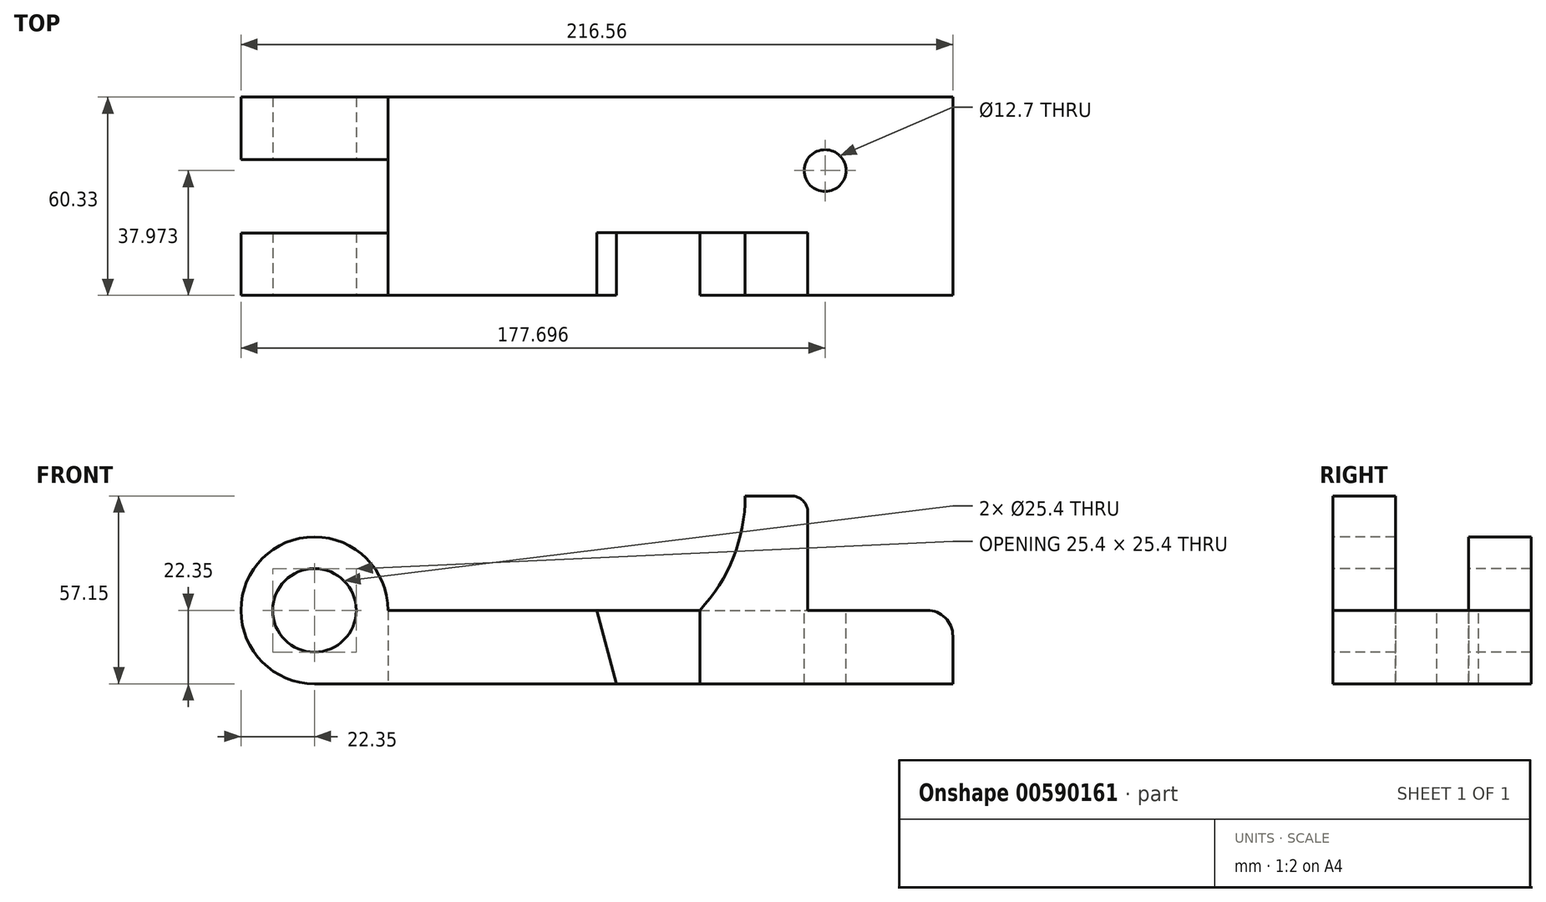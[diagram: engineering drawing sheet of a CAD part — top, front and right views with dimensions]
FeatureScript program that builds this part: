
annotation { "Feature Type Name" : "Feature", "Feature Type Description" : "" }
export const myFeature = defineFeature(function(context is Context, id is Id, definition is map)
    precondition{}
    {
        {
            var Q0;
            Q0=qCreatedBy(makeId("Front.planeOp"),FACE);
            var sketch = newSketch(context, id + "F0", { "sketchPlane" : qUnion([Q0])});
            skCircle(sketch, "E0", {"center": v(0, 0) * mm, "radius": 22.35 * mm});
            skCircle(sketch, "E1", {"center": v(0, 0) * mm, "radius": 12.7 * mm});
            skLineSegment(sketch, "E2", {"start": v(0, -22.35) * mm, "end": v(91.85, -22.35) * mm});
            skLineSegment(sketch, "E3", {"start": v(91.85, -22.35) * mm, "end": v(117.25, -22.35) * mm});
            skLineSegment(sketch, "E4", {"start": v(117.25, -22.35) * mm, "end": v(194.2, -22.35) * mm});
            skLineSegment(sketch, "E5", {"start": v(0, 62.8) * mm, "end": v(0, -59.04) * mm, "construction": true});
            skLineSegment(sketch, "E6", {"start": v(22.35, 0) * mm, "end": v(85.85, 0) * mm});
            skLineSegment(sketch, "E7", {"start": v(85.85, 0) * mm, "end": v(91.85, -22.35) * mm});
            skLineSegment(sketch, "E8", {"start": v(117.25, 0) * mm, "end": v(117.25, -22.35) * mm});
            skLineSegment(sketch, "E9", {"start": v(85.85, 0) * mm, "end": v(117.25, 0) * mm});
            skPoint(sketch, "E10", {"position": v(-22.35, 0) * mm});
            skLineSegment(sketch, "E11", {"start": v(194.2, -22.35) * mm, "end": v(194.2, -7.87) * mm});
            skPoint(sketch, "E11.endSnap0", {"position": v(54.1, 0) * mm});
            skLineSegment(sketch, "E12", {"start": v(186.33, 0) * mm, "end": v(150.09, 0) * mm});
            skLineSegment(sketch, "E13", {"start": v(150.09, 0) * mm, "end": v(150.09, 29.72) * mm});
            skLineSegment(sketch, "E14", {"start": v(145, 34.8) * mm, "end": v(131.04, 34.8) * mm});
            skArc(sketch, "E15", {"start": v(117.25, 0) * mm, "mid": v(127.46, 16.08) * mm, "end": v(131.04, 34.8) * mm});
            skPoint(sketch, "E16.visualSharp", {"position": v(150.09, 34.8) * mm});
            skArc(sketch, "E16.filletArc", {"start": v(150.09, 29.72) * mm, "mid": v(148.6, 33.31) * mm, "end": v(145, 34.8) * mm});
            skPoint(sketch, "E17.visualSharp", {"position": v(194.2, 0) * mm});
            skArc(sketch, "E17.filletArc", {"start": v(194.2, -7.87) * mm, "mid": v(191.9, -2.3) * mm, "end": v(186.33, 0) * mm});
            skLineSegment(sketch, "E18", {"start": v(117.25, 0) * mm, "end": v(150.09, 0) * mm});
            skSolve(sketch);
        }
        {
            var Q0;
            Q0=makeQuery(id+"F0.imprint","IMPRINT",FACE,{"disambiguationData":[TD([[makeQuery(id+"F0.imprint","IMPRINT",EDGE,{"derivedFrom":sQuery(id+"F0.wireOp",EDGE,"E1")}),-1.0]])]});
            extrude(context, id + "F1", {"entities" : qUnion([Q0]), "oppositeDirection" : true, "depth" : 60.32 * mm, "offsetDistance" : 25.4 * mm});
        }
        {
            var Q0;
            Q0=makeQuery(id+"F0.imprint","IMPRINT",FACE,{"disambiguationData":[TD([[makeQuery(id+"F0.imprint","IMPRINT",EDGE,{"derivedFrom":sQuery(id+"F0.wireOp",EDGE,"E4")}),1.0]])]});
            var Q1;
            {var subQ0=sQuery(id+"F0.wireOp",EDGE,"E2");Q1=makeQuery(id+"F0.imprint","IMPRINT",FACE,{"disambiguationData":[TD([[makeQuery(id+"F0.imprint","IMPRINT",EDGE,{"derivedFrom":subQ0}),1.0]])]});}
            extrude(context, id + "F2", {"entities" : qUnion([Q0, Q1]), "operationType" : NewBodyOperationType.ADD, "oppositeDirection" : true, "depth" : 60.32 * mm, "offsetDistance" : 25.4 * mm});
        }
        {
            var Q0;
            Q0=makeQuery(id+"F0.imprint","IMPRINT",FACE,{"disambiguationData":[TD([[makeQuery(id+"F0.imprint","IMPRINT",EDGE,{"derivedFrom":sQuery(id+"F0.wireOp",EDGE,"E3")}),1.0]])]});
            var Q1;
            Q1=makeQuery(id+"F2.opExtrude","CAP_VERTEX",VERTEX,{"disambiguationData":[OSD([sQuery(id+"F0.wireOp",EDGE,"E8"),sQuery(id+"F0.wireOp",EDGE,"E9"),sQuery(id+"F0.wireOp",EDGE,"E15")])],"isStart":false});
            extrude(context, id + "F3", {"entities" : qUnion([Q0]), "operationType" : NewBodyOperationType.ADD, "endBound" : BoundingType.UP_TO_VERTEX, "oppositeDirection" : true, "depth" : 97.03 * mm, "endBoundEntityVertex" : qUnion([Q1]), "offsetDistance" : 25.4 * mm});
        }
        {
            var Q0;
            Q0=makeQuery(id+"F0.imprint","IMPRINT",FACE,{"disambiguationData":[TD([[makeQuery(id+"F0.imprint","IMPRINT",EDGE,{"derivedFrom":sQuery(id+"F0.wireOp",EDGE,"E3")}),1.0]])]});
            extrude(context, id + "F4", {"entities" : qUnion([Q0]), "operationType" : NewBodyOperationType.REMOVE, "oppositeDirection" : true, "depth" : 19.05 * mm, "offsetDistance" : 25.4 * mm});
        }
        {
            var Q0;
            Q0=makeQuery(id+"F0.imprint","IMPRINT",FACE,{"disambiguationData":[TD([[makeQuery(id+"F0.imprint","IMPRINT",EDGE,{"derivedFrom":sQuery(id+"F0.wireOp",EDGE,"E13")}),1.0]])]});
            extrude(context, id + "F5", {"entities" : qUnion([Q0]), "operationType" : NewBodyOperationType.ADD, "oppositeDirection" : true, "depth" : 19.05 * mm, "offsetDistance" : 25.4 * mm});
        }
        {
            var Q0;
            Q0=qCreatedBy(makeId("Top.planeOp"),FACE);
            var sketch = newSketch(context, id + "F6", { "sketchPlane" : qUnion([Q0])});
            skLineSegment(sketch, "E19", {"start": v(22.35, 0) * mm, "end": v(22.35, 60.33) * mm});
            skLineSegment(sketch, "E20", {"start": v(-22.35, 0) * mm, "end": v(-22.35, 19) * mm, "construction": true});
            skLineSegment(sketch, "E21", {"start": v(-22.35, 60.33) * mm, "end": v(-22.35, 41.33) * mm, "construction": true});
            skLineSegment(sketch, "E22", {"start": v(-22.35, 41.33) * mm, "end": v(22.35, 41.33) * mm});
            skLineSegment(sketch, "E23", {"start": v(-22.35, 41.33) * mm, "end": v(-22.35, 19) * mm});
            skLineSegment(sketch, "E24", {"start": v(22.35, 19) * mm, "end": v(22.35, 41.33) * mm});
            skLineSegment(sketch, "E25", {"start": v(-22.35, 19) * mm, "end": v(22.35, 19) * mm});
            skSolve(sketch);
        }
        {
            var Q0;
            Q0=qSketchRegion(id+"F6",true);
            extrude(context, id + "F7", {"entities" : qUnion([Q0]), "operationType" : NewBodyOperationType.REMOVE, "depth" : 73.66 * mm, "offsetDistance" : 25.4 * mm, "symmetric" : true});
        }
        {
            var Q0;
            Q0=makeQuery(id+"F3.boolean.opBoolean","MERGE",FACE,{"derivedFrom":[makeQuery(id+"F2.opExtrude","SWEPT_FACE",FACE,{"disambiguationData":[OSD([sQuery(id+"F0.wireOp",EDGE,"E6")])]}),makeQuery(id+"F2.opExtrude","SWEPT_FACE",FACE,{"disambiguationData":[OSD([sQuery(id+"F0.wireOp",EDGE,"E12"),sQuery(id+"F0.wireOp",EDGE,"E18")])]}),makeQuery(id+"F3.opExtrude","SWEPT_FACE",FACE,{"disambiguationData":[OSD([sQuery(id+"F0.wireOp",EDGE,"E9")])]})]});
            var sketch = newSketch(context, id + "F8", { "sketchPlane" : qUnion([Q0])});
            skLineSegment(sketch, "E26.0", {"start": v(194.2, 60.33) * mm, "end": v(186.33, 60.33) * mm});
            skLineSegment(sketch, "E27", {"start": v(194.2, 60.33) * mm, "end": v(155.35, 60.33) * mm, "construction": true});
            skLineSegment(sketch, "E28", {"start": v(155.35, 60.33) * mm, "end": v(155.35, 37.97) * mm, "construction": true});
            skCircle(sketch, "E29", {"center": v(155.35, 37.97) * mm, "radius": 6.35 * mm});
            skSolve(sketch);
        }
        {
            var Q0;
            Q0=qSketchRegion(id+"F8",true);
            extrude(context, id + "F9", {"entities" : qUnion([Q0]), "operationType" : NewBodyOperationType.REMOVE, "oppositeDirection" : true, "depth" : 25.4 * mm, "offsetDistance" : 25.4 * mm});
        }
    });
